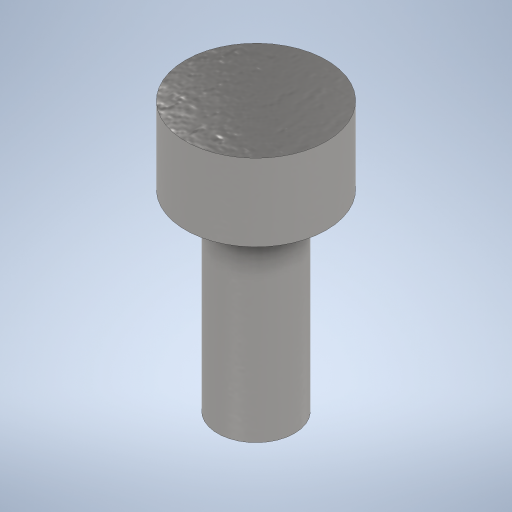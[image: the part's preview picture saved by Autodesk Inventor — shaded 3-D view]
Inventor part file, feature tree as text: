
AUTODESK INVENTOR PART (.ipt)
format: ipt  version: 2024 (Build 280153000, 153)  size: 260,608 bytes
history: native  units: mm
features: extrude x2, sketch x2
ambient origin geometry x8: Origin, YZ Plane, XZ Plane, XY Plane, X Axis, Y Axis, Z Axis, Center Point
bodies: Solid1 (feature_tree)
feature tree (4):
  extrude  "Extrusion1"  Depth=3.0mm TaperAngle=0.0deg
  extrude  "Extrusion2"  Depth=7.5mm TaperAngle=0.0deg
  sketch  "Sketch1"  dims[d0=5.5mm d1=3.0mm d2=0.0mm]
  sketch  "Sketch2"  dims[d3=3.0mm d4=7.5mm d5=0.0mm]
